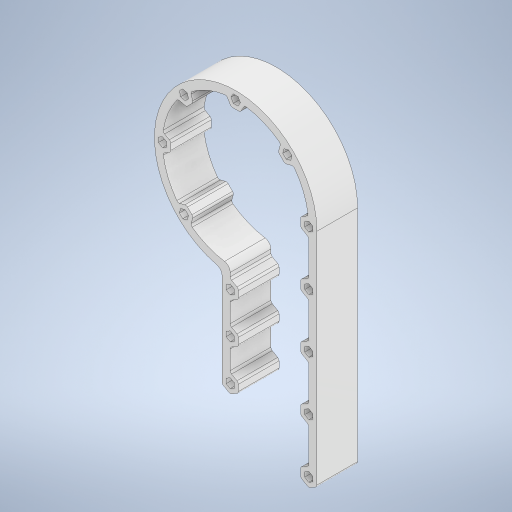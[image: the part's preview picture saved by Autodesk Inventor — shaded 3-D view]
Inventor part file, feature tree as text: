
AUTODESK INVENTOR PART (.ipt)
format: ipt  version: 2024.3 (Build 283343000, 343)  size: 933,376 bytes
history: native  units: mm
features: sketch x9, extrude x6, fillet x5, hole x3, other x1
ambient origin geometry x8: Origin, YZ Plane, XZ Plane, XY Plane, X Axis, Y Axis, Z Axis, Center Point
bodies: Body1 (feature_tree)
feature tree (24):
  other  "ソリッド1"
  extrude  "押し出し1"  Depth=120.0mm
  hole  "穴1"  [1 undecoded]
  extrude  "押し出し3"  Depth=92.0mm
  extrude  "押し出し10"  TaperAngle=22.5deg  [1 undecoded]
  hole  "穴8"  [1 undecoded]
  fillet  "フィレット4"  Radius=60.0mm
  hole  "穴13"  [1 undecoded]
  fillet  "フィレット11"  Radius=210.0mm
  extrude  "押し出し17"  Depth=210.0mm
  extrude  "押し出し18"  Depth=3.0mm TaperAngle=0.0deg
  fillet  "フィレット15"  [1 undecoded]
  fillet  "フィレット16"  Radius=14.835299mm
  fillet  "フィレット17"  Radius=14.835299mm
  extrude  "押し出し19"  Depth=60.0mm
  sketch  "スケッチ1"
  sketch  "スケッチ2"
  sketch  "スケッチ4"
  sketch  "スケッチ17"
  sketch  "スケッチ20"
  sketch  "スケッチ28"
  sketch  "スケッチ32"
  sketch  "スケッチ33"
  sketch  "スケッチ34"
note: 5 required parameter values undecoded (feature->parameter linkage not recoverable at this tier; creation-order binding heuristic only, values carry confidence <= 0.55)
